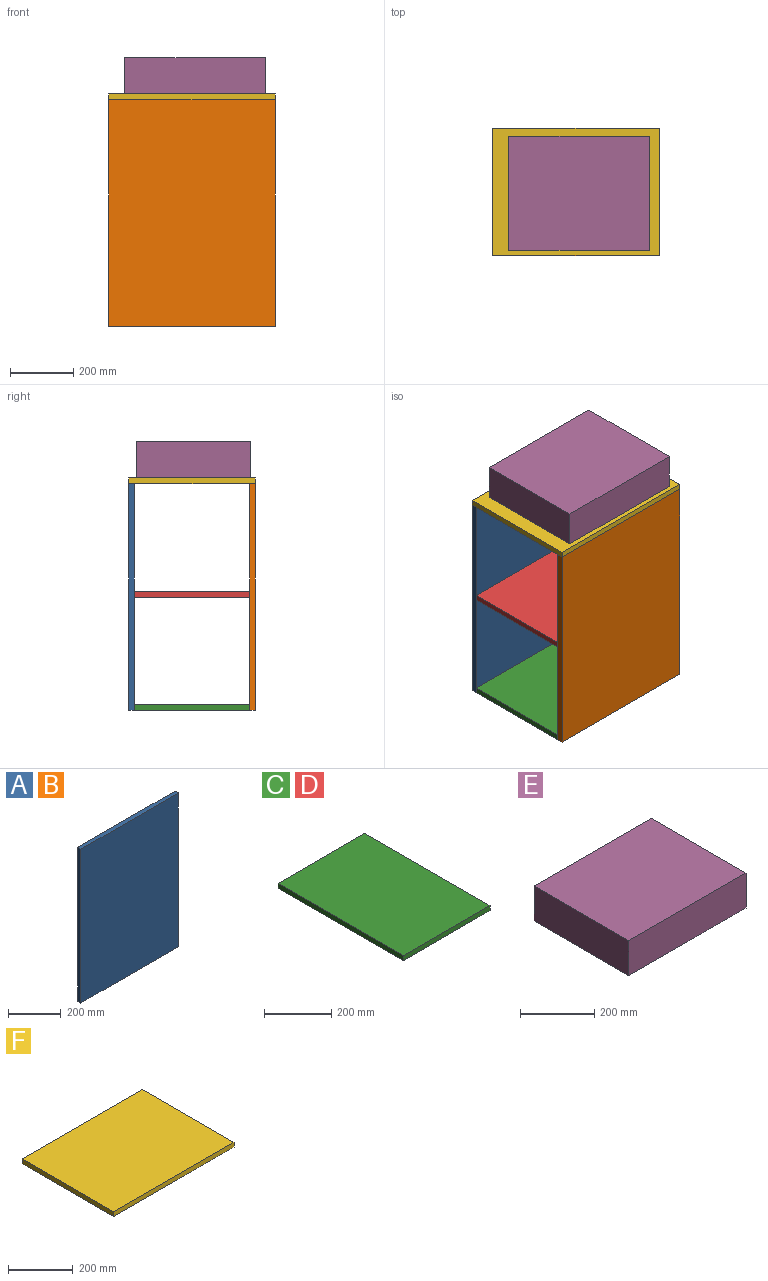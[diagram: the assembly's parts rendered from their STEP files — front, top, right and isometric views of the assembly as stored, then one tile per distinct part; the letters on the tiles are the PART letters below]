
ASSEMBLY  parts=6 mates=12
PART A: 6 faces, bbox 525x18x716 mm
  f0: plane 716x18mm, normal (-1,0,0), area 12888mm2, adj f1,f3,f4,f5
  f1: plane 525x18mm, normal (0,0,-1), area 9450mm2, adj f0,f2,f4,f5
  f2: plane 716x18mm, normal (1,0,0), area 12888mm2, adj f1,f3,f4,f5
  f3: plane 525x18mm, normal (0,0,1), area 9450mm2, adj f0,f2,f4,f5
  f4: plane 716x525mm, normal (0,-1,0), area 375900mm2, adj f0,f1,f2,f3
  f5: plane 716x525mm, normal (0,1,0), area 375900mm2, adj f0,f1,f2,f3
PART B: same geometry as A
PART C: 6 faces, bbox 364x525x18 mm
  f0: plane 364x18mm, normal (0,-1,0), area 6552mm2, adj f1,f3,f4,f5
  f1: plane 525x18mm, normal (1,0,0), area 9450mm2, adj f0,f2,f4,f5
  f2: plane 364x18mm, normal (0,1,0), area 6552mm2, adj f1,f3,f4,f5
  f3: plane 525x18mm, normal (-1,0,0), area 9450mm2, adj f0,f2,f4,f5
  f4: plane 525x364mm, normal (0,0,1), area 191100mm2, adj f0,f1,f2,f3
  f5: plane 525x364mm, normal (0,0,-1), area 191100mm2, adj f0,f1,f2,f3
PART D: same geometry as C
PART E: 6 faces, bbox 445x360x115 mm
  f0: plane 445x115mm, normal (0,-1,0), area 51175mm2, adj f1,f3,f4,f5
  f1: plane 360x115mm, normal (1,0,0), area 41400mm2, adj f0,f2,f4,f5
  f2: plane 445x115mm, normal (0,1,0), area 51175mm2, adj f1,f3,f4,f5
  f3: plane 360x115mm, normal (-1,0,0), area 41400mm2, adj f0,f2,f4,f5
  f4: plane 445x360mm, normal (0,0,1), area 160200mm2, adj f0,f1,f2,f3
  f5: plane 445x360mm, normal (0,0,-1), area 160200mm2, adj f0,f1,f2,f3
PART F: 6 faces, bbox 525x400x18 mm
  f0: plane 400x18mm, normal (-1,0,0), area 7200mm2, adj f1,f3,f4,f5
  f1: plane 525x18mm, normal (0,-1,0), area 9450mm2, adj f0,f2,f4,f5
  f2: plane 400x18mm, normal (1,0,0), area 7200mm2, adj f1,f3,f4,f5
  f3: plane 525x18mm, normal (0,1,0), area 9450mm2, adj f0,f2,f4,f5
  f4: plane 525x400mm, normal (0,0,1), area 210000mm2, adj f0,f1,f2,f3
  f5: plane 525x400mm, normal (0,0,-1), area 210000mm2, adj f0,f1,f2,f3
PLACE A t=(-111.04,0,238.98)mm
PLACE B t=(-111.04,-382,238.98)mm
PLACE C rot(axis=(0,0,-1),90deg) t=(50.79,-710.94,-716)mm
PLACE D rot(axis=(0.71,0.71,0),180deg) t=(50.79,310.94,-340)mm
PLACE E t=(135.79,511.38,18)mm
PLACE F at identity fixed
MATE planar A.f3 <-> F.f5  axis (0,0,1) through (262.5,-9,0)mm
MATE planar F.f0 <-> B.f0  axis (-1,0,0) through (0,-200,9)mm
MATE planar A.f5 <-> F.f3  axis (0,1,0) through (0,0,0)mm
MATE planar C.f5 <-> A.f1  axis (0,0,-1) through (262.5,-200,-716)mm
MATE planar C.f3 <-> A.f4  axis (0,1,0) through (262.5,-18,-707)mm
MATE planar F.f0 <-> A.f0  axis (-1,0,0) through (0,-200,9)mm
MATE planar F.f4 <-> E.f5  axis (0,0,1) through (262.5,-200,18)mm
MATE planar A.f4 <-> D.f1  axis (0,-1,0) through (262.5,-18,-358)mm
MATE planar D.f2 <-> B.f2  axis (1,0,0) through (525,-200,-349)mm
MATE planar B.f3 <-> F.f5  axis (0,0,1) through (262.5,-391,0)mm
MATE planar D.f3 <-> B.f5  axis (0,-1,0) through (262.5,-382,-340)mm
MATE planar C.f0 <-> D.f0  axis (-1,0,0) through (0,-200,-707)mm
